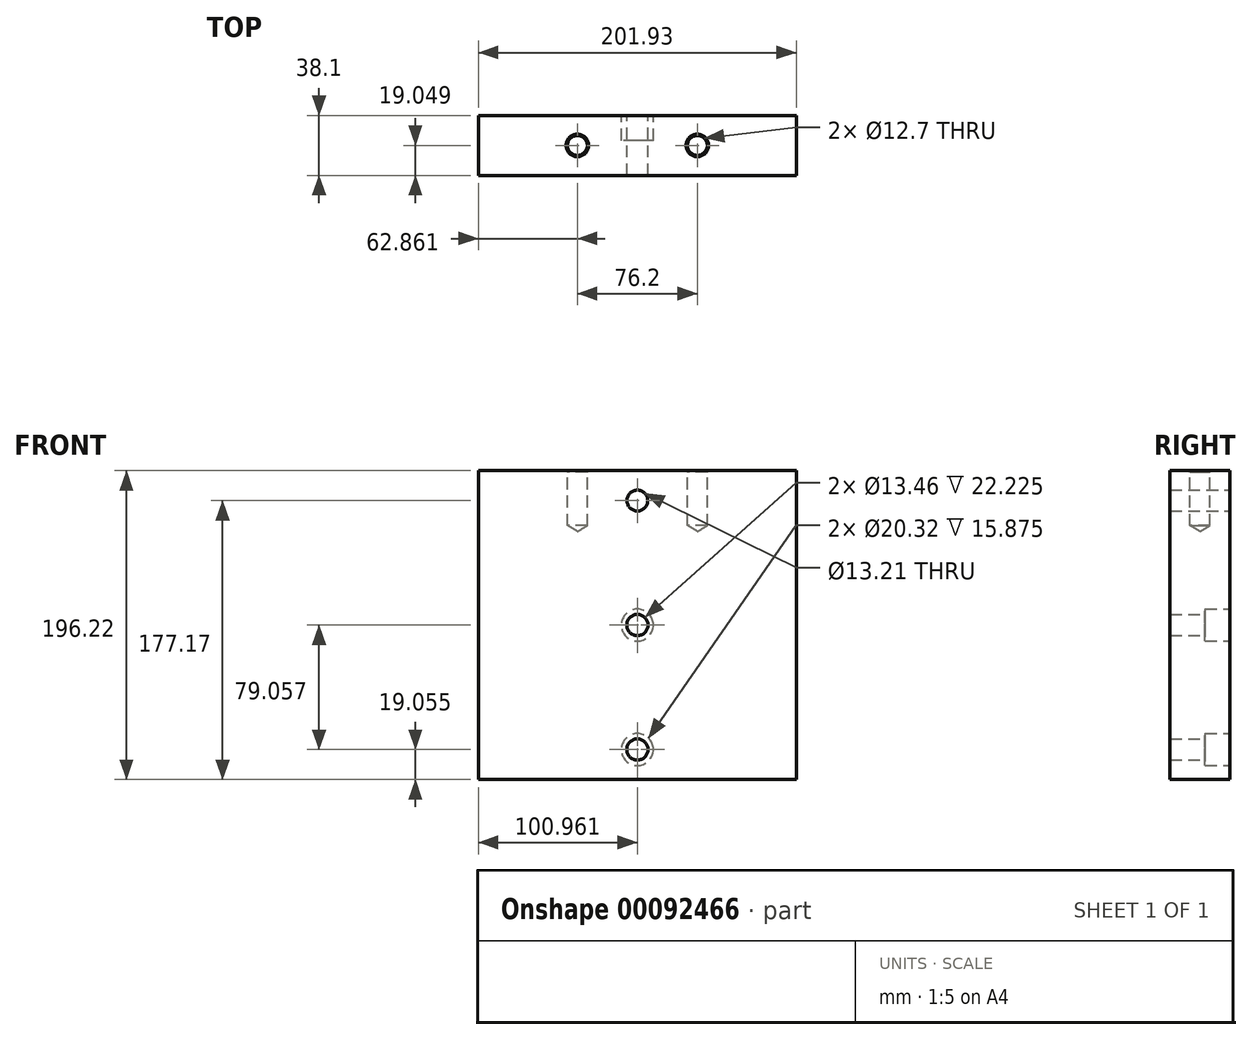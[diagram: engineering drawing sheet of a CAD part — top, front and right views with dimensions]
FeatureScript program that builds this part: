
annotation { "Feature Type Name" : "Feature", "Feature Type Description" : "" }
export const myFeature = defineFeature(function(context is Context, id is Id, definition is map)
    precondition{}
    {
        {
            var Q0;
            Q0=qCreatedBy(makeId("Top.planeOp"),FACE);
            var sketch = newSketch(context, id + "F0", { "sketchPlane" : qUnion([Q0])});
            skCircle(sketch, "E0", {"center": v(-846.13, -154.24) * mm, "radius": 101.6 * mm});
            skLineSegment(sketch, "E1", {"start": v(855.8, 198.6) * mm, "end": v(653.87, 198.6) * mm});
            skLineSegment(sketch, "E2", {"start": v(855.8, 160.5) * mm, "end": v(855.8, 198.6) * mm});
            skLineSegment(sketch, "E3", {"start": v(653.87, 198.6) * mm, "end": v(653.87, 160.5) * mm});
            skCircle(sketch, "E4", {"center": v(685.93, -42.2) * mm, "radius": 6.73 * mm});
            skCircle(sketch, "E5", {"center": v(-912.8, -154.24) * mm, "radius": 6.73 * mm});
            skCircle(sketch, "E6", {"center": v(685.93, 24.48) * mm, "radius": 6.73 * mm});
            skCircle(sketch, "E7", {"center": v(-779.46, -154.24) * mm, "radius": 6.73 * mm});
            skLineSegment(sketch, "E8", {"start": v(845.28, 41.94) * mm, "end": v(652.24, 41.94) * mm});
            skCircle(sketch, "E9", {"center": v(830.04, -46.96) * mm, "radius": 6.53 * mm});
            skCircle(sketch, "E10", {"center": v(830.04, 29.24) * mm, "radius": 6.53 * mm});
            skLineSegment(sketch, "E11", {"start": v(653.87, 160.5) * mm, "end": v(855.8, 160.5) * mm});
            skLineSegment(sketch, "E12", {"start": v(-541.33, -52.64) * mm, "end": v(-465.13, -52.64) * mm});
            skLineSegment(sketch, "E13", {"start": v(-503.23, -245.68) * mm, "end": v(-465.13, -245.68) * mm});
            skLineSegment(sketch, "E14", {"start": v(-541.33, -205.25) * mm, "end": v(-465.13, -205.25) * mm});
            skLineSegment(sketch, "E15", {"start": v(-268.92, -217.74) * mm, "end": v(-268.92, -78.04) * mm});
            skLineSegment(sketch, "E16", {"start": v(-541.33, -61.27) * mm, "end": v(-479.42, -61.27) * mm});
            skLineSegment(sketch, "E17", {"start": v(-479.42, -74.48) * mm, "end": v(-541.33, -74.48) * mm});
            skLineSegment(sketch, "E18", {"start": v(-465.13, -78.04) * mm, "end": v(-479.42, -78.04) * mm});
            skLineSegment(sketch, "E19", {"start": v(-479.42, -57.72) * mm, "end": v(-465.13, -57.72) * mm});
            skLineSegment(sketch, "E20", {"start": v(-479.42, -78.04) * mm, "end": v(-479.42, -74.48) * mm});
            skLineSegment(sketch, "E21", {"start": v(-479.42, -74.48) * mm, "end": v(-479.42, -67.88) * mm});
            skLineSegment(sketch, "E22", {"start": v(-479.42, -67.88) * mm, "end": v(-479.42, -61.27) * mm});
            skLineSegment(sketch, "E23", {"start": v(-479.42, -61.27) * mm, "end": v(-479.42, -57.72) * mm});
            skLineSegment(sketch, "E24", {"start": v(-541.33, -218.7) * mm, "end": v(-465.13, -218.7) * mm});
            skLineSegment(sketch, "E25", {"start": v(-268.92, -78.04) * mm, "end": v(-465.13, -78.04) * mm});
            skLineSegment(sketch, "E26", {"start": v(-465.13, -116.14) * mm, "end": v(-268.92, -116.14) * mm});
            skLineSegment(sketch, "E27", {"start": v(-465.13, -217.74) * mm, "end": v(-268.92, -217.74) * mm});
            skLineSegment(sketch, "E28", {"start": v(-488.95, -100.9) * mm, "end": v(-503.23, -100.9) * mm});
            skLineSegment(sketch, "E29", {"start": v(-488.95, -100.9) * mm, "end": v(-488.95, -80.58) * mm});
            skLineSegment(sketch, "E30", {"start": v(-427.03, -97.09) * mm, "end": v(-488.95, -97.09) * mm});
            skLineSegment(sketch, "E31", {"start": v(-488.95, -84.39) * mm, "end": v(-427.03, -84.39) * mm});
            skLineSegment(sketch, "E32", {"start": v(-503.23, -80.58) * mm, "end": v(-488.95, -80.58) * mm});
            skLineSegment(sketch, "E33", {"start": v(-427.03, -97.09) * mm, "end": v(-427.03, -84.39) * mm});
            skLineSegment(sketch, "E34", {"start": v(-488.95, -142.17) * mm, "end": v(-503.23, -142.17) * mm});
            skLineSegment(sketch, "E35", {"start": v(-488.95, -142.17) * mm, "end": v(-488.95, -121.85) * mm});
            skLineSegment(sketch, "E36", {"start": v(-427.03, -138.36) * mm, "end": v(-488.95, -138.36) * mm});
            skLineSegment(sketch, "E37", {"start": v(-488.95, -125.66) * mm, "end": v(-427.03, -125.66) * mm});
            skLineSegment(sketch, "E38", {"start": v(-503.23, -121.85) * mm, "end": v(-488.95, -121.85) * mm});
            skLineSegment(sketch, "E39", {"start": v(-427.03, -138.36) * mm, "end": v(-427.03, -125.66) * mm});
            skLineSegment(sketch, "E40", {"start": v(-488.95, -212.02) * mm, "end": v(-503.23, -212.02) * mm});
            skLineSegment(sketch, "E41", {"start": v(-488.95, -212.02) * mm, "end": v(-488.95, -191.7) * mm});
            skLineSegment(sketch, "E42", {"start": v(-427.03, -208.21) * mm, "end": v(-488.95, -208.21) * mm});
            skLineSegment(sketch, "E43", {"start": v(-488.95, -195.51) * mm, "end": v(-427.03, -195.51) * mm});
            skLineSegment(sketch, "E44", {"start": v(-503.23, -191.7) * mm, "end": v(-488.95, -191.7) * mm});
            skLineSegment(sketch, "E45", {"start": v(-427.03, -208.21) * mm, "end": v(-427.03, -195.51) * mm});
            skLineSegment(sketch, "E46", {"start": v(652.24, -59.66) * mm, "end": v(652.24, 41.94) * mm});
            skLineSegment(sketch, "E47", {"start": v(653.87, 249.4) * mm, "end": v(653.87, 445.62) * mm});
            skLineSegment(sketch, "E48", {"start": v(-446.08, -112.96) * mm, "end": v(-484.18, -112.96) * mm});
            skLineSegment(sketch, "E49", {"start": v(-484.18, -106.61) * mm, "end": v(-446.08, -106.61) * mm});
            skLineSegment(sketch, "E50", {"start": v(-484.18, -112.96) * mm, "end": v(-484.18, -106.61) * mm});
            skLineSegment(sketch, "E51", {"start": v(-446.08, -106.61) * mm, "end": v(-446.08, -112.96) * mm});
            skLineSegment(sketch, "E52", {"start": v(-465.13, -245.68) * mm, "end": v(-465.13, -52.64) * mm});
            skLineSegment(sketch, "E53", {"start": v(-541.33, -255.84) * mm, "end": v(-541.33, -52.64) * mm});
            skLineSegment(sketch, "E54", {"start": v(-465.13, 99.13) * mm, "end": v(-503.23, 99.13) * mm});
            skLineSegment(sketch, "E55", {"start": v(855.8, 249.4) * mm, "end": v(855.8, 445.62) * mm});
            skLineSegment(sketch, "E56", {"start": v(-503.23, 200.73) * mm, "end": v(-465.13, 200.73) * mm});
            skLineSegment(sketch, "E57", {"start": v(855.8, 445.62) * mm, "end": v(653.87, 445.62) * mm});
            skLineSegment(sketch, "E58", {"start": v(-541.33, 251.53) * mm, "end": v(-503.23, 251.53) * mm});
            skLineSegment(sketch, "E59", {"start": v(-541.33, 48.33) * mm, "end": v(-541.33, 251.53) * mm});
            skLineSegment(sketch, "E60", {"start": v(-503.23, 48.33) * mm, "end": v(-541.33, 48.33) * mm});
            skLineSegment(sketch, "E61", {"start": v(-503.23, 48.33) * mm, "end": v(-503.23, 251.53) * mm});
            skCircle(sketch, "E62", {"center": v(754.83, 268.46) * mm, "radius": 10.16 * mm});
            skCircle(sketch, "E63", {"center": v(754.83, 426.57) * mm, "radius": 10.16 * mm});
            skCircle(sketch, "E64", {"center": v(754.83, 347.52) * mm, "radius": 10.16 * mm});
            skCircle(sketch, "E65", {"center": v(754.83, 268.46) * mm, "radius": 6.6 * mm});
            skCircle(sketch, "E66", {"center": v(754.83, 347.52) * mm, "radius": 6.6 * mm});
            skCircle(sketch, "E67", {"center": v(754.83, 426.57) * mm, "radius": 6.6 * mm});
            skLineSegment(sketch, "E68", {"start": v(-745.17, -78.04) * mm, "end": v(-947.1, -78.04) * mm});
            skLineSegment(sketch, "E69", {"start": v(-745.17, -116.14) * mm, "end": v(-745.17, -78.04) * mm});
            skLineSegment(sketch, "E70", {"start": v(-947.1, -78.04) * mm, "end": v(-947.1, -116.14) * mm});
            skLineSegment(sketch, "E71", {"start": v(-947.1, -116.14) * mm, "end": v(-745.17, -116.14) * mm});
            skCircle(sketch, "E72", {"center": v(716.73, 179.56) * mm, "radius": 6.35 * mm});
            skCircle(sketch, "E73", {"center": v(792.93, 179.56) * mm, "radius": 6.35 * mm});
            skLineSegment(sketch, "E74", {"start": v(-465.13, 250.9) * mm, "end": v(-268.92, 250.9) * mm});
            skLineSegment(sketch, "E75", {"start": v(-465.13, 250.9) * mm, "end": v(-465.13, 48.96) * mm});
            skLineSegment(sketch, "E76", {"start": v(-465.13, 48.96) * mm, "end": v(-268.92, 48.96) * mm});
            skLineSegment(sketch, "E77", {"start": v(-268.92, 48.96) * mm, "end": v(-268.92, 250.9) * mm});
            skLineSegment(sketch, "E78", {"start": v(751.52, -407.52) * mm, "end": v(947.73, -407.52) * mm});
            skLineSegment(sketch, "E79", {"start": v(751.52, -407.52) * mm, "end": v(751.52, -445.62) * mm});
            skCircle(sketch, "E80", {"center": v(770.57, -426.57) * mm, "radius": 10.16 * mm});
            skCircle(sketch, "E81", {"center": v(928.68, -426.57) * mm, "radius": 10.16 * mm});
            skCircle(sketch, "E82", {"center": v(849.63, -426.57) * mm, "radius": 10.16 * mm});
            skCircle(sketch, "E83", {"center": v(770.57, -426.57) * mm, "radius": 6.6 * mm});
            skCircle(sketch, "E84", {"center": v(849.63, -426.57) * mm, "radius": 6.6 * mm});
            skCircle(sketch, "E85", {"center": v(928.68, -426.57) * mm, "radius": 6.6 * mm});
            skLineSegment(sketch, "E86", {"start": v(653.87, 249.4) * mm, "end": v(855.8, 249.4) * mm});
            skLineSegment(sketch, "E87", {"start": v(-465.13, 168.98) * mm, "end": v(-268.92, 168.98) * mm});
            skLineSegment(sketch, "E88", {"start": v(-268.92, 130.88) * mm, "end": v(-465.13, 130.88) * mm});
            skLineSegment(sketch, "E89", {"start": v(-367.03, 149.93) * mm, "end": v(-268.92, 149.93) * mm});
            skLineSegment(sketch, "E90", {"start": v(-465.13, 149.93) * mm, "end": v(-367.03, 149.93) * mm});
            skCircle(sketch, "E91", {"center": v(-446.08, 149.93) * mm, "radius": 10.16 * mm});
            skCircle(sketch, "E92", {"center": v(-287.97, 149.93) * mm, "radius": 10.16 * mm});
            skCircle(sketch, "E93", {"center": v(-367.03, 149.93) * mm, "radius": 10.16 * mm});
            skCircle(sketch, "E94", {"center": v(-446.08, 149.93) * mm, "radius": 6.6 * mm});
            skCircle(sketch, "E95", {"center": v(-367.03, 149.93) * mm, "radius": 6.6 * mm});
            skCircle(sketch, "E96", {"center": v(-287.97, 149.93) * mm, "radius": 6.6 * mm});
            skLineSegment(sketch, "E97", {"start": v(947.73, -407.52) * mm, "end": v(947.73, -445.62) * mm});
            skLineSegment(sketch, "E98", {"start": v(947.73, -445.62) * mm, "end": v(751.52, -445.62) * mm});
            skLineSegment(sketch, "E99", {"start": v(700.72, -407.52) * mm, "end": v(700.72, -445.62) * mm});
            skCircle(sketch, "E100", {"center": v(800.83, 29.24) * mm, "radius": 6.35 * mm});
            skCircle(sketch, "E101", {"center": v(800.83, -46.96) * mm, "radius": 6.35 * mm});
            skCircle(sketch, "E102", {"center": v(696.05, -8.86) * mm, "radius": 6.35 * mm});
            skCircle(sketch, "E103", {"center": v(765.9, -8.86) * mm, "radius": 6.35 * mm});
            skLineSegment(sketch, "E104", {"start": v(599.12, -445.62) * mm, "end": v(599.12, -407.52) * mm});
            skLineSegment(sketch, "E105", {"start": v(700.72, -407.52) * mm, "end": v(599.12, -407.52) * mm});
            skLineSegment(sketch, "E106", {"start": v(700.72, -445.62) * mm, "end": v(599.12, -445.62) * mm});
            skCircle(sketch, "E107", {"center": v(615, -426.57) * mm, "radius": 6.35 * mm});
            skCircle(sketch, "E108", {"center": v(684.84, -426.57) * mm, "radius": 6.35 * mm});
            skLineSegment(sketch, "E109", {"start": v(-827.08, -217.74) * mm, "end": v(-865.18, -217.74) * mm});
            skCircle(sketch, "E110", {"center": v(-812.8, -211.98) * mm, "radius": 6.73 * mm});
            skCircle(sketch, "E111", {"center": v(-879.47, -211.98) * mm, "radius": 6.73 * mm});
            skLineSegment(sketch, "E112", {"start": v(-795.33, -52.64) * mm, "end": v(-896.93, -52.64) * mm});
            skLineSegment(sketch, "E113", {"start": v(-896.93, -52.64) * mm, "end": v(-896.93, -245.68) * mm});
            skLineSegment(sketch, "E114", {"start": v(-795.33, -52.64) * mm, "end": v(-795.33, -245.68) * mm});
            skLineSegment(sketch, "E115", {"start": v(-865.18, -116.14) * mm, "end": v(-865.18, -217.74) * mm});
            skCircle(sketch, "E116", {"center": v(-808.03, -67.88) * mm, "radius": 6.53 * mm});
            skCircle(sketch, "E117", {"center": v(-884.23, -67.88) * mm, "radius": 6.53 * mm});
            skLineSegment(sketch, "E118", {"start": v(-827.08, -116.14) * mm, "end": v(-827.08, -217.74) * mm});
            skCircle(sketch, "E119", {"center": v(-879.47, -96.5) * mm, "radius": 6.73 * mm});
            skCircle(sketch, "E120", {"center": v(-812.8, -96.5) * mm, "radius": 6.73 * mm});
            skLineSegment(sketch, "E121", {"start": v(-846.13, -78.04) * mm, "end": v(-846.13, -116.14) * mm});
            skCircle(sketch, "E122", {"center": v(-808.03, -97.09) * mm, "radius": 6.35 * mm});
            skCircle(sketch, "E123", {"center": v(-884.23, -97.09) * mm, "radius": 6.35 * mm});
            skLineSegment(sketch, "E124", {"start": v(-846.13, -217.74) * mm, "end": v(-846.13, -116.14) * mm});
            skCircle(sketch, "E125", {"center": v(-846.13, -201.86) * mm, "radius": 6.35 * mm});
            skCircle(sketch, "E126", {"center": v(-846.13, -132.01) * mm, "radius": 6.35 * mm});
            skCircle(sketch, "E127", {"center": v(696.05, -8.86) * mm, "radius": 10.16 * mm});
            skCircle(sketch, "E128", {"center": v(765.9, -8.86) * mm, "radius": 10.16 * mm});
            skCircle(sketch, "E129", {"center": v(800.83, 29.24) * mm, "radius": 10.16 * mm});
            skCircle(sketch, "E130", {"center": v(800.83, -46.96) * mm, "radius": 10.16 * mm});
            skCircle(sketch, "E131", {"center": v(830.04, 29.24) * mm, "radius": 10.16 * mm});
            skCircle(sketch, "E132", {"center": v(830.04, -46.96) * mm, "radius": 10.16 * mm});
            skCircle(sketch, "E133", {"center": v(685.93, -191.42) * mm, "radius": 6.73 * mm});
            skCircle(sketch, "E134", {"center": v(685.93, -258.1) * mm, "radius": 6.73 * mm});
            skLineSegment(sketch, "E135", {"start": v(845.28, -97.76) * mm, "end": v(845.28, -135.86) * mm});
            skLineSegment(sketch, "E136", {"start": v(845.28, -275.56) * mm, "end": v(652.24, -275.56) * mm});
            skLineSegment(sketch, "E137", {"start": v(845.28, -173.96) * mm, "end": v(652.24, -173.96) * mm});
            skCircle(sketch, "E138", {"center": v(830.04, -186.66) * mm, "radius": 6.53 * mm});
            skCircle(sketch, "E139", {"center": v(830.04, -262.86) * mm, "radius": 6.53 * mm});
            skCircle(sketch, "E140", {"center": v(800.83, -262.86) * mm, "radius": 6.35 * mm});
            skCircle(sketch, "E141", {"center": v(800.83, -186.66) * mm, "radius": 6.35 * mm});
            skCircle(sketch, "E142", {"center": v(696.05, -224.76) * mm, "radius": 6.35 * mm});
            skCircle(sketch, "E143", {"center": v(765.9, -224.76) * mm, "radius": 6.35 * mm});
            skCircle(sketch, "E144", {"center": v(800.83, -262.86) * mm, "radius": 10.16 * mm});
            skCircle(sketch, "E145", {"center": v(800.83, -186.66) * mm, "radius": 10.16 * mm});
            skCircle(sketch, "E146", {"center": v(765.9, -224.76) * mm, "radius": 10.16 * mm});
            skCircle(sketch, "E147", {"center": v(696.05, -224.76) * mm, "radius": 10.16 * mm});
            skCircle(sketch, "E148", {"center": v(830.04, -186.66) * mm, "radius": 10.16 * mm});
            skCircle(sketch, "E149", {"center": v(830.04, -262.86) * mm, "radius": 10.16 * mm});
            skLineSegment(sketch, "E150", {"start": v(845.28, -173.96) * mm, "end": v(845.28, -275.56) * mm});
            skLineSegment(sketch, "E151", {"start": v(652.24, -97.76) * mm, "end": v(845.28, -97.76) * mm});
            skLineSegment(sketch, "E152", {"start": v(692.66, -97.76) * mm, "end": v(692.66, -135.86) * mm});
            skLineSegment(sketch, "E153", {"start": v(836.64, -97.76) * mm, "end": v(836.64, -121.57) * mm});
            skLineSegment(sketch, "E154", {"start": v(823.43, -121.57) * mm, "end": v(823.43, -97.76) * mm});
            skLineSegment(sketch, "E155", {"start": v(819.88, -135.86) * mm, "end": v(819.88, -121.57) * mm});
            skLineSegment(sketch, "E156", {"start": v(840.2, -121.57) * mm, "end": v(840.2, -135.86) * mm});
            skLineSegment(sketch, "E157", {"start": v(819.88, -121.57) * mm, "end": v(823.43, -121.57) * mm});
            skLineSegment(sketch, "E158", {"start": v(823.43, -121.57) * mm, "end": v(830.04, -121.57) * mm});
            skLineSegment(sketch, "E159", {"start": v(830.04, -121.57) * mm, "end": v(836.64, -121.57) * mm});
            skLineSegment(sketch, "E160", {"start": v(836.64, -121.57) * mm, "end": v(840.2, -121.57) * mm});
            skLineSegment(sketch, "E161", {"start": v(679.2, -97.76) * mm, "end": v(679.2, -135.86) * mm});
            skLineSegment(sketch, "E162", {"start": v(790.67, -112.05) * mm, "end": v(790.67, -97.76) * mm});
            skLineSegment(sketch, "E163", {"start": v(790.67, -112.05) * mm, "end": v(810.99, -112.05) * mm});
            skLineSegment(sketch, "E164", {"start": v(794.48, -135.86) * mm, "end": v(794.48, -112.05) * mm});
            skLineSegment(sketch, "E165", {"start": v(807.18, -112.05) * mm, "end": v(807.18, -135.86) * mm});
            skLineSegment(sketch, "E166", {"start": v(810.99, -97.76) * mm, "end": v(810.99, -112.05) * mm});
            skLineSegment(sketch, "E167", {"start": v(755.74, -112.05) * mm, "end": v(755.74, -97.76) * mm});
            skLineSegment(sketch, "E168", {"start": v(755.74, -112.05) * mm, "end": v(776.06, -112.05) * mm});
            skLineSegment(sketch, "E169", {"start": v(759.55, -135.86) * mm, "end": v(759.55, -112.05) * mm});
            skLineSegment(sketch, "E170", {"start": v(772.25, -112.05) * mm, "end": v(772.25, -135.86) * mm});
            skLineSegment(sketch, "E171", {"start": v(776.06, -97.76) * mm, "end": v(776.06, -112.05) * mm});
            skLineSegment(sketch, "E172", {"start": v(759.55, -173.96) * mm, "end": v(772.25, -173.96) * mm});
            skLineSegment(sketch, "E173", {"start": v(685.9, -112.05) * mm, "end": v(685.9, -97.76) * mm});
            skLineSegment(sketch, "E174", {"start": v(685.9, -112.05) * mm, "end": v(706.21, -112.05) * mm});
            skLineSegment(sketch, "E175", {"start": v(689.7, -135.86) * mm, "end": v(689.7, -112.05) * mm});
            skLineSegment(sketch, "E176", {"start": v(702.4, -112.05) * mm, "end": v(702.4, -135.86) * mm});
            skLineSegment(sketch, "E177", {"start": v(706.21, -97.76) * mm, "end": v(706.21, -112.05) * mm});
            skLineSegment(sketch, "E178", {"start": v(689.7, -173.96) * mm, "end": v(702.4, -173.96) * mm});
            skLineSegment(sketch, "E179", {"start": v(652.24, -135.86) * mm, "end": v(845.28, -135.86) * mm});
            skLineSegment(sketch, "E180", {"start": v(652.24, -59.66) * mm, "end": v(845.28, -59.66) * mm});
            skLineSegment(sketch, "E181", {"start": v(845.28, -59.66) * mm, "end": v(845.28, 41.94) * mm});
            skLineSegment(sketch, "E182", {"start": v(652.24, -135.86) * mm, "end": v(652.24, -97.76) * mm});
            skLineSegment(sketch, "E183", {"start": v(652.24, -275.56) * mm, "end": v(652.24, -173.96) * mm});
            skLineSegment(sketch, "E184", {"start": v(-795.33, -245.68) * mm, "end": v(-896.93, -245.68) * mm});
            skLineSegment(sketch, "E185", {"start": v(-503.23, -255.84) * mm, "end": v(-503.23, -52.64) * mm});
            skLineSegment(sketch, "E186", {"start": v(-503.23, -255.84) * mm, "end": v(-541.33, -255.84) * mm});
            skLineSegment(sketch, "E187", {"start": v(685.93, 24.48) * mm, "end": v(696.05, -8.86) * mm});
            skLineSegment(sketch, "E188", {"start": v(696.05, -8.86) * mm, "end": v(685.93, -42.2) * mm});
            skLineSegment(sketch, "E189", {"start": v(685.93, -42.2) * mm, "end": v(765.9, -8.86) * mm});
            skLineSegment(sketch, "E190", {"start": v(765.9, -8.86) * mm, "end": v(800.83, 29.24) * mm});
            skLineSegment(sketch, "E191", {"start": v(800.83, -46.96) * mm, "end": v(830.04, -46.96) * mm});
            skLineSegment(sketch, "E192", {"start": v(830.04, -46.96) * mm, "end": v(830.04, 29.24) * mm});
            skLineSegment(sketch, "E193", {"start": v(800.83, 29.24) * mm, "end": v(830.04, 29.24) * mm});
            skLineSegment(sketch, "E194", {"start": v(642.71, -69.19) * mm, "end": v(642.71, 51.46) * mm});
            skLineSegment(sketch, "E195", {"start": v(854.8, 51.46) * mm, "end": v(854.8, -69.19) * mm});
            skLineSegment(sketch, "E196", {"start": v(800.83, 29.24) * mm, "end": v(800.83, -46.96) * mm});
            skLineSegment(sketch, "E197", {"start": v(765.9, -8.86) * mm, "end": v(696.05, -8.86) * mm});
            skLineSegment(sketch, "E198", {"start": v(685.93, 24.48) * mm, "end": v(685.93, -42.2) * mm});
            skLineSegment(sketch, "E199", {"start": v(685.93, -42.2) * mm, "end": v(830.04, -46.96) * mm});
            skSolve(sketch);
        }
        {
            var Q0;
            Q0=makeQuery(id+"F0.imprint","IMPRINT",FACE,{"disambiguationData":[TD([[makeQuery(id+"F0.imprint","IMPRINT",EDGE,{"derivedFrom":sQuery(id+"F0.wireOp",EDGE,"E47")}),-1.0]])]});
            var Q1;
            Q1=makeQuery(id+"F0.imprint","IMPRINT",FACE,{"disambiguationData":[TD([[makeQuery(id+"F0.imprint","IMPRINT",EDGE,{"derivedFrom":sQuery(id+"F0.wireOp",EDGE,"E63")}),-1.0]])]});
            var Q2;
            Q2=makeQuery(id+"F0.imprint","IMPRINT",FACE,{"disambiguationData":[TD([[makeQuery(id+"F0.imprint","IMPRINT",EDGE,{"derivedFrom":sQuery(id+"F0.wireOp",EDGE,"E64")}),-1.0]])]});
            var Q3;
            Q3=makeQuery(id+"F0.imprint","IMPRINT",FACE,{"disambiguationData":[TD([[makeQuery(id+"F0.imprint","IMPRINT",EDGE,{"derivedFrom":sQuery(id+"F0.wireOp",EDGE,"E66")}),-1.0]])]});
            var Q4;
            Q4=makeQuery(id+"F0.imprint","IMPRINT",FACE,{"disambiguationData":[TD([[makeQuery(id+"F0.imprint","IMPRINT",EDGE,{"derivedFrom":sQuery(id+"F0.wireOp",EDGE,"E67")}),-1.0]])]});
            var Q5;
            Q5=makeQuery(id+"F0.imprint","IMPRINT",FACE,{"disambiguationData":[TD([[makeQuery(id+"F0.imprint","IMPRINT",EDGE,{"derivedFrom":sQuery(id+"F0.wireOp",EDGE,"E62")}),-1.0]])]});
            var Q6;
            Q6=makeQuery(id+"F0.imprint","IMPRINT",FACE,{"disambiguationData":[TD([[makeQuery(id+"F0.imprint","IMPRINT",EDGE,{"derivedFrom":sQuery(id+"F0.wireOp",EDGE,"E65")}),-1.0]])]});
            extrude(context, id + "F1", {"entities" : qUnion([Q0, Q1, Q2, Q3, Q4, Q5, Q6]), "oppositeDirection" : true, "depth" : 38.1 * mm});
        }
        {
            var Q0;
            Q0=sQuery(id+"F0.wireOp",VERTEX,"E63.center");
            var Q1;
            Q1=sQuery(id+"F0.wireOp",VERTEX,"E64.center");
            var Q2;
            Q2=makeQuery(id+"F1.opExtrude","SWEPT_BODY",BODY,{"disambiguationData":[OSD([sQuery(id+"F0.wireOp",EDGE,"E47"),sQuery(id+"F0.wireOp",EDGE,"E55"),sQuery(id+"F0.wireOp",EDGE,"E57"),sQuery(id+"F0.wireOp",EDGE,"E86")])]});
            hole(context, id + "F2", {"style" : HoleStyle.C_BORE, "endStyle" : HoleEndStyle.BLIND, "holeDiameter" : 13.46 * mm, "cBoreDiameter" : 20.32 * mm, "cBoreDepth" : 15.88 * mm, "holeDepth" : 50.8 * mm, "startFromSketch" : true, "locations" : qUnion([Q0, Q1]), "scope" : qUnion([Q2])});
        }
        {
            var Q0;
            Q0=makeQuery(id+"F1.opExtrude","SWEPT_BODY",BODY,{"disambiguationData":[OSD([sQuery(id+"F0.wireOp",EDGE,"E47"),sQuery(id+"F0.wireOp",EDGE,"E55"),sQuery(id+"F0.wireOp",EDGE,"E57"),sQuery(id+"F0.wireOp",EDGE,"E86")])]});
            var Q1;
            Q1=sQuery(id+"F0.wireOp",EDGE,"E86");
            transform(context, id + "F3", {"entities" : qUnion([Q0]), "transformType" : TransformType.ROTATION, "transformAxis" : qUnion([Q1]), "angle" : 90 * degree, "oppositeDirection" : true, "makeCopy" : false});
        }
        {
            var Q0;
            Q0=makeQuery(id+"F1.opExtrude","SWEPT_BODY",BODY,{"disambiguationData":[OSD([sQuery(id+"F0.wireOp",EDGE,"E47"),sQuery(id+"F0.wireOp",EDGE,"E55"),sQuery(id+"F0.wireOp",EDGE,"E57"),sQuery(id+"F0.wireOp",EDGE,"E86")])]});
            var Q1;
            Q1=sQuery(id+"F0.wireOp",VERTEX,"E86.start");
            var Q2;
            Q2=sQuery(id+"F0.wireOp",VERTEX,"E3.start");
            transform(context, id + "F4", {"entities" : qUnion([Q0]), "transformType" : TransformType.TRANSLATION_ENTITY, "oppositeDirectionEntity" : false, "transformLine" : qUnion([Q1, Q2]), "makeCopy" : false});
        }
        {
            var Q0;
            Q0=sQuery(id+"F0.wireOp",VERTEX,"E72.center");
            var Q1;
            Q1=sQuery(id+"F0.wireOp",VERTEX,"E73.center");
            var Q2;
            Q2=makeQuery(id+"F1.opExtrude","SWEPT_BODY",BODY,{"disambiguationData":[OSD([sQuery(id+"F0.wireOp",EDGE,"E47"),sQuery(id+"F0.wireOp",EDGE,"E55"),sQuery(id+"F0.wireOp",EDGE,"E57"),sQuery(id+"F0.wireOp",EDGE,"E86")])]});
            hole(context, id + "F5", {"style" : HoleStyle.C_SINK, "endStyle" : HoleEndStyle.BLIND, "holeDiameter" : 12.7 * mm, "cSinkDiameter" : 14.29 * mm, "cSinkAngle" : 90 * degree, "holeDepth" : 34.92 * mm, "startFromSketch" : true, "locations" : qUnion([Q0, Q1]), "scope" : qUnion([Q2])});
        }
    });
